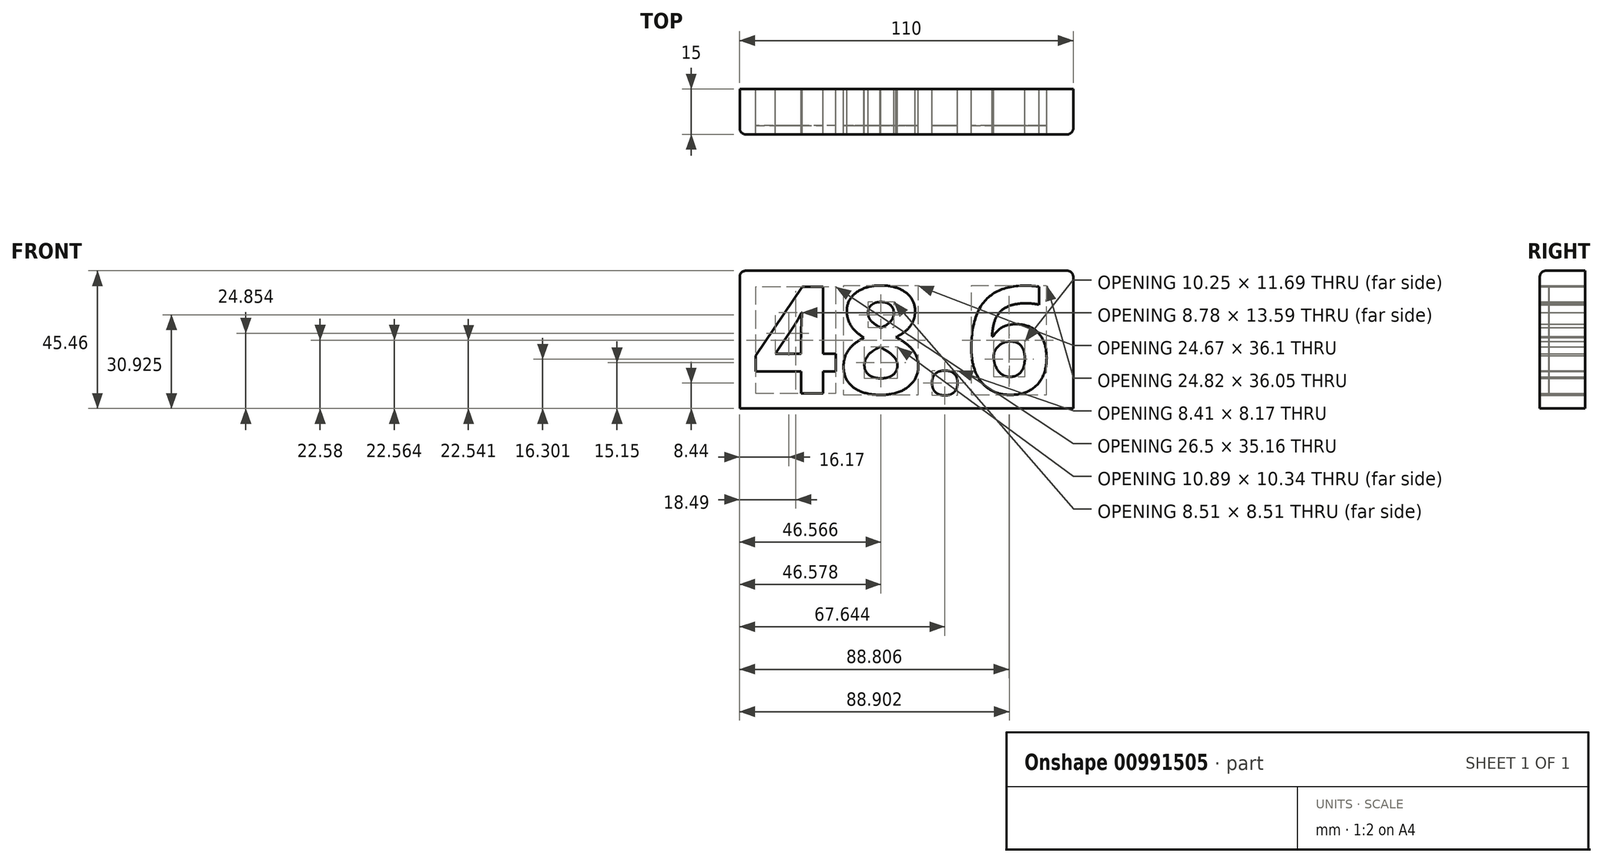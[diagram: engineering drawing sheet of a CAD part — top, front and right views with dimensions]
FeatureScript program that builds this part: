
annotation { "Feature Type Name" : "Feature", "Feature Type Description" : "" }
export const myFeature = defineFeature(function(context is Context, id is Id, definition is map)
    precondition{}
    {
        {
            var Q0;
            Q0=qCreatedBy(makeId("Front.planeOp"),FACE);
            var sketch = newSketch(context, id + "F0", { "sketchPlane" : qUnion([Q0])});
            skText(sketch, "E0", { "text": "48.6", "fontName": "OpenSans-Bold.ttf"});
            skLineSegment(sketch, "E1.bottom", {"start": v(-54.4, 28) * mm, "end": v(55.6, 28) * mm});
            skLineSegment(sketch, "E1.top", {"start": v(-54.4, -17.47) * mm, "end": v(55.6, -17.47) * mm});
            skLineSegment(sketch, "E1.left", {"start": v(-54.4, 28) * mm, "end": v(-54.4, -17.47) * mm});
            skLineSegment(sketch, "E1.right", {"start": v(55.6, 28) * mm, "end": v(55.6, -17.47) * mm});
            const initialGuessF0  = {"E0": [-0.05, -0.01247, 1, 0, 0.03546]};
            skSetInitialGuess(sketch, initialGuessF0);
            skSolve(sketch);
        }
        {
            var Q0;
            Q0=makeQuery(id+"F0.imprint","IMPRINT",FACE,{"disambiguationData":[TD([[makeQuery(id+"F0.imprint","IMPRINT",EDGE,{"derivedFrom":sQuery(id+"F0.wireOp",EDGE,"E0.sketch_text.stroke-0")}),1.0]])]});
            var Q1;
            Q1=makeQuery(id+"F0.imprint","IMPRINT",FACE,{"disambiguationData":[TD([[makeQuery(id+"F0.imprint","IMPRINT",EDGE,{"derivedFrom":sQuery(id+"F0.wireOp",EDGE,"E0.sketch_text.stroke-41")}),1.0]])]});
            var Q2;
            Q2=makeQuery(id+"F0.imprint","IMPRINT",FACE,{"disambiguationData":[TD([[makeQuery(id+"F0.imprint","IMPRINT",EDGE,{"derivedFrom":sQuery(id+"F0.wireOp",EDGE,"E0.sketch_text.stroke-34")}),1.0]])]});
            var Q3;
            Q3=makeQuery(id+"F0.imprint","IMPRINT",FACE,{"disambiguationData":[TD([[makeQuery(id+"F0.imprint","IMPRINT",EDGE,{"derivedFrom":sQuery(id+"F0.wireOp",EDGE,"E0.sketch_text.stroke-11")}),1.0]])]});
            var Q4;
            Q4=makeQuery(id+"F0.imprint","IMPRINT",FACE,{"disambiguationData":[TD([[makeQuery(id+"F0.imprint","IMPRINT",EDGE,{"derivedFrom":sQuery(id+"F0.wireOp",EDGE,"E0.sketch_text.stroke-74")}),1.0]])]});
            extrude(context, id + "F1", {"entities" : qUnion([Q0, Q1, Q2, Q3, Q4]), "depth" : 15 * mm, "offsetDistance" : 25 * mm});
        }
        {
            var Q0;
            Q0=makeQuery(id+"F0.imprint","IMPRINT",FACE,{"disambiguationData":[TD([[makeQuery(id+"F0.imprint","IMPRINT",EDGE,{"derivedFrom":sQuery(id+"F0.wireOp",EDGE,"E0.sketch_text.stroke-0")}),-1.0]])]});
            var Q1;
            Q1=makeQuery(id+"F0.imprint","IMPRINT",FACE,{"disambiguationData":[TD([[makeQuery(id+"F0.imprint","IMPRINT",EDGE,{"derivedFrom":sQuery(id+"F0.wireOp",EDGE,"E0.sketch_text.stroke-18")}),-1.0]])]});
            var Q2;
            Q2=makeQuery(id+"F0.imprint","IMPRINT",FACE,{"disambiguationData":[TD([[makeQuery(id+"F0.imprint","IMPRINT",EDGE,{"derivedFrom":sQuery(id+"F0.wireOp",EDGE,"E0.sketch_text.stroke-49")}),-1.0]])]});
            var Q3;
            Q3=makeQuery(id+"F0.imprint","IMPRINT",FACE,{"disambiguationData":[TD([[makeQuery(id+"F0.imprint","IMPRINT",EDGE,{"derivedFrom":sQuery(id+"F0.wireOp",EDGE,"E0.sketch_text.stroke-57")}),-1.0]])]});
            extrude(context, id + "F2", {"entities" : qUnion([Q0, Q1, Q2, Q3]), "depth" : 12 * mm, "offsetDistance" : 25 * mm});
        }
        {
            var Q0;
            Q0=makeQuery(id+"F1.opExtrude","CAP_EDGE",EDGE,{"disambiguationData":[OSD([sQuery(id+"F0.wireOp",EDGE,"E1.bottom")])],"isStart":false});
            var Q1;
            Q1=makeQuery(id+"F1.opExtrude","SWEPT_EDGE",EDGE,{"disambiguationData":[OSD([sQuery(id+"F0.wireOp",EDGE,"E1.bottom"),sQuery(id+"F0.wireOp",EDGE,"E1.left")])]});
            var Q2;
            Q2=makeQuery(id+"F1.opExtrude","CAP_EDGE",EDGE,{"disambiguationData":[OSD([sQuery(id+"F0.wireOp",EDGE,"E1.left")])],"isStart":false});
            var Q3;
            Q3=makeQuery(id+"F1.opExtrude","CAP_EDGE",EDGE,{"disambiguationData":[OSD([sQuery(id+"F0.wireOp",EDGE,"E1.right")])],"isStart":false});
            var Q4;
            Q4=makeQuery(id+"F1.opExtrude","SWEPT_EDGE",EDGE,{"disambiguationData":[OSD([sQuery(id+"F0.wireOp",EDGE,"E1.bottom"),sQuery(id+"F0.wireOp",EDGE,"E1.right")])]});
            fillet(context, id + "F3", {"entities" : qUnion([Q0, Q1, Q2, Q3, Q4]), "radius" : 2 * mm, "tangentPropagation" : true, "allowEdgeOverflow" : false});
        }
    });
